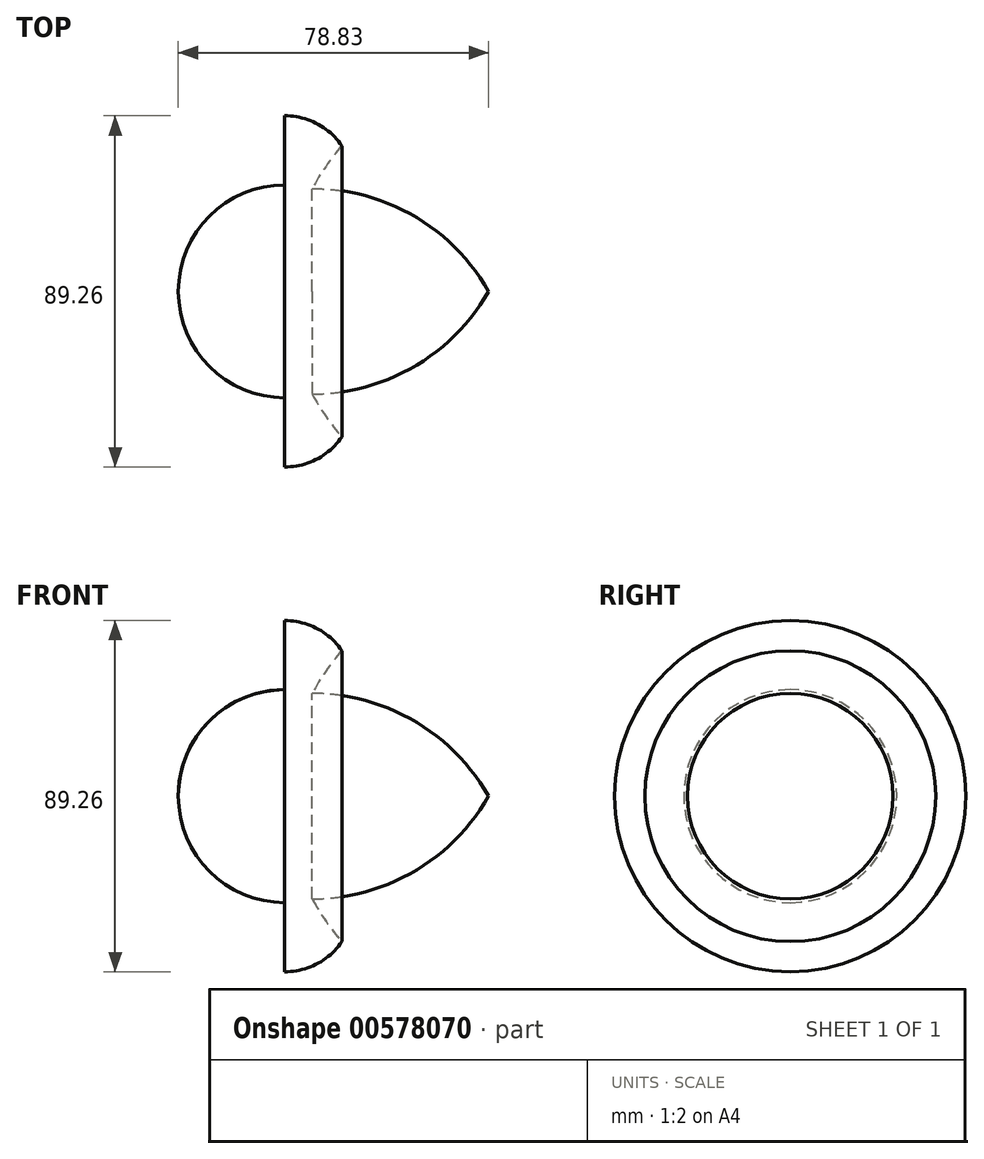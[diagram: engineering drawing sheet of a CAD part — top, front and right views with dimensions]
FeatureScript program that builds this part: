
annotation { "Feature Type Name" : "Feature", "Feature Type Description" : "" }
export const myFeature = defineFeature(function(context is Context, id is Id, definition is map)
    precondition{}
    {
        {
            var Q0;
            Q0=qCreatedBy(makeId("Front.planeOp"),FACE);
            var sketch = newSketch(context, id + "F0", { "sketchPlane" : qUnion([Q0])});
            skArc(sketch, "E0", {"start": v(-27.05, 0) * mm, "mid": v(-19.13, -19.13) * mm, "end": v(0, -27.05) * mm});
            skArc(sketch, "E1", {"start": v(14.52, -36.95) * mm, "mid": v(8.21, -42.59) * mm, "end": v(0, -44.63) * mm});
            skLineSegment(sketch, "E2", {"start": v(0, -27.05) * mm, "end": v(0, -44.63) * mm});
            skArc(sketch, "E3", {"start": v(14.52, -36.95) * mm, "mid": v(10.42, -31.75) * mm, "end": v(6.97, -26.1) * mm});
            skArc(sketch, "E4", {"start": v(6.97, -26.1) * mm, "mid": v(32.9, -19.1) * mm, "end": v(51.78, 0) * mm});
            skLineSegment(sketch, "E5", {"start": v(51.78, 0) * mm, "end": v(-27.05, 0) * mm});
            skSolve(sketch);
        }
        {
            var Q0;
            Q0=makeQuery(id+"F0.imprint","IMPRINT",FACE,{"disambiguationData":[TD([[makeQuery(id+"F0.imprint","IMPRINT",EDGE,{"derivedFrom":sQuery(id+"F0.wireOp",EDGE,"E0")}),1.0]])]});
            var Q1;
            Q1=sQuery(id+"F0.wireOp",EDGE,"E5");
            revolve(context, id + "F1", {"entities" : qUnion([Q0]), "axis" : qUnion([Q1]), "revolveType" : RevolveType.FULL});
        }
    });
